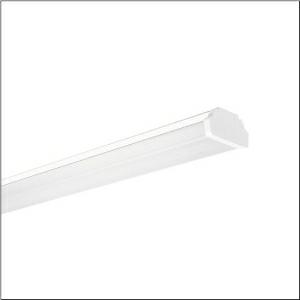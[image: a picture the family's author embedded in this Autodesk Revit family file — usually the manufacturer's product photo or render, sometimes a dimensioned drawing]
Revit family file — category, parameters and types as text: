
# Revit family: dus_31_gen_2_53bd811dv4a5c2_c54e
name_source: partatom
category: Lighting Fixtures
units: mm (PartAtom-declared; Revit-internal decimal feet)

## family parameters
Cut with Voids When Loaded = No
Host = Face
Light Source = No
Part Type = Normal
Room Calculation Point = No
Round Connector Dimension = Use Diameter
Shared = No

## types (1)
- --- (1 x LED, 10860 lm, 61.4 W, 4000K)
    Apparent Load = 61 VA
    CIE Flux Codes = 50 78 94 90 100
    Color Rendering = 80
    Color Temperature = 4000K
    Default Elevation = 1800 mm
    Description = DUS 31 Gen.2, luminaire insert, of sheet steel, coil coated, white, length: 1.535mm, width: 81mm, height: 90mm, 5x system unit, system units: 307mm, LED rated luminous flux: 10.860lm, light colour: 840, SDCM (Standard Deviation of Colour Matching)MacAdam ≤ 3 SDCM (initial), control gear: DALI 2, control gear: ECG DALI, with plug, 5-pole, with phase selection, mains connection: 220..240V, AC, 50/60Hz, rated input power: 61W, through-wiring accessed according to module size, primary optical cover: cover, of PMMA, light emission: direct distribution, primary light characteristic: symmetric, protection rating (complete): IP20, protection rating (LED compartment): IP50, insulation class (complete): insulation class I (protective earthing), certification: CE, ENEC, VDE, UKCA, impact resistance: IK03, permissible ambient temperature for indoor applications: -25..+35°C, corresponds to IFS (International Featured Standards) requirements for safety and quality in the food industry, reducing of maximum allowable ambient temperature of 5°C with ceiling mounting, packaging unit: 1 piece
    Height = 95 mm
    Lamp = 1 x LED
    Lamp Light Flux = 10860 lm
    Lamp Power = 61.4 W
    Lamp count = 1
    Length = 1535 mm
    Luminous efficacy = 177 lm/W
    Manufacturer = Siteco
    ModVariant = No
    Model = 53BD811DV4A5C2
    Mounting Place = Ceiling
    Mounting Type = Pendant
    Number of Poles = 1
    OnlyDefault = Yes
    Power Factor = 1
    Product Name = DUS 31 Gen.2
    Product group = luminaire insert | ceiling pendant
    ProductGroupID = 901
    Protection Class = Protection class I
    Protection Degree = IP 20
    RLX_Detail_Level = 1
    RLX_Emergency_Light_Flux = 0 lm
    RLX_Emergency_Type = 0
    RLX_Emergency_Type_DB = No
    RlxData = <blob elided: 32225 chars, md5=ac91e66a>
    Socket = socket
    Standby Power = 0 W
    System Light Flux = 10860 lm
    System Power = 61 W
    Type Comments = factory setting: luminous flux: 100 % | dim-lin: 254 | 418 mA
    Type Image = l_1319596.jpg
    URL = http://relux.com
    VarID = @adj_050221
    Voltage = 0 V
    Weight = 0.00 kg
    Width = 81 mm

## geometry (parser evidence)
native form markers: Blend x4, Sweep x12
no freeform markers — native parametric forms only
